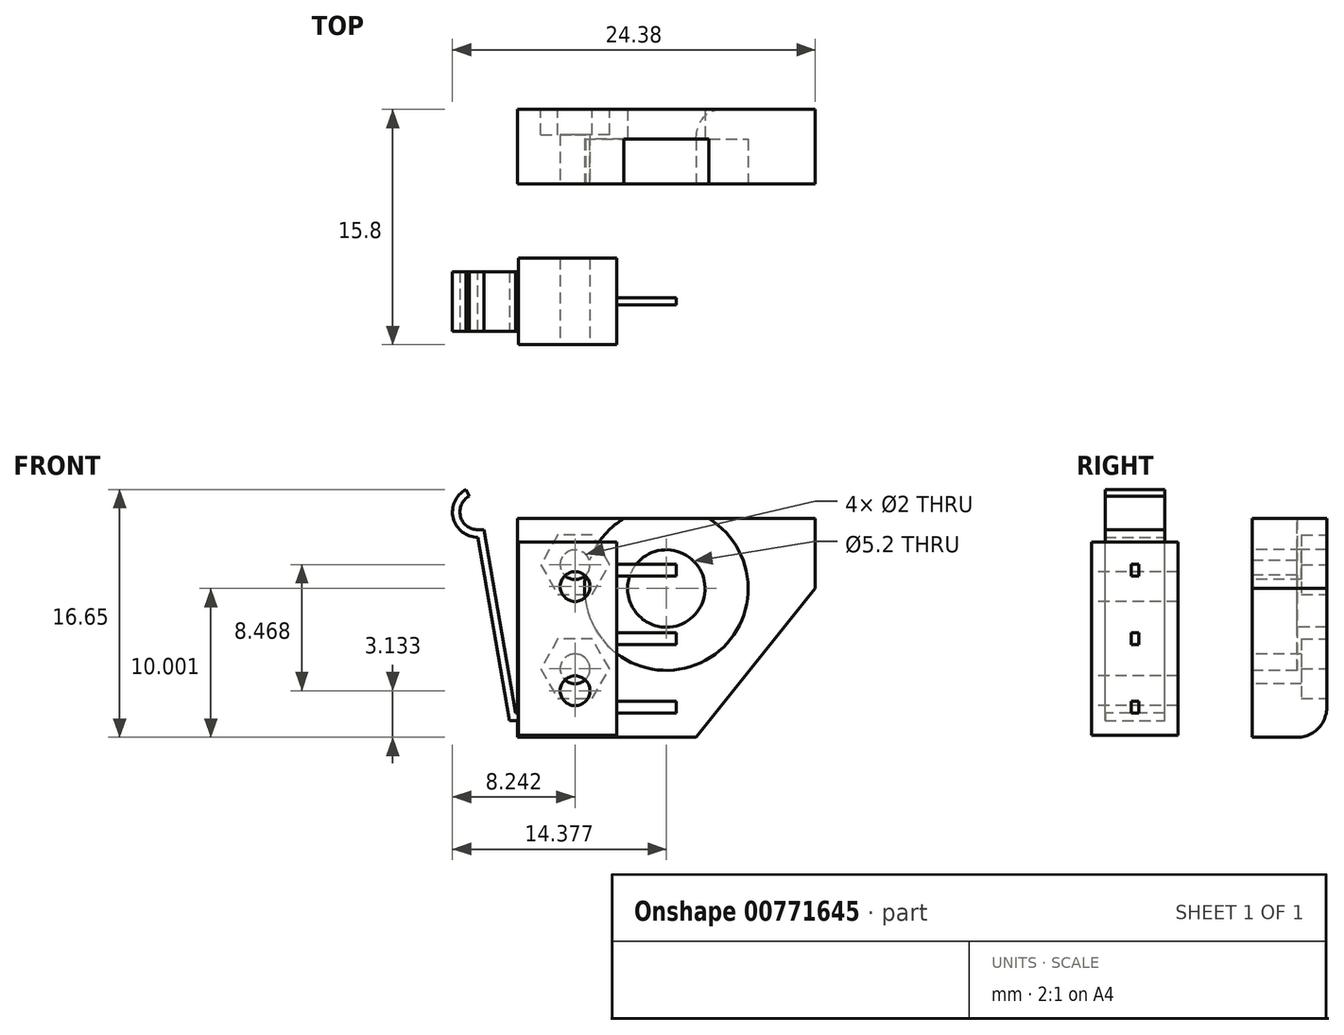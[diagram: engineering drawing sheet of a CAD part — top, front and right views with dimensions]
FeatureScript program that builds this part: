
annotation { "Feature Type Name" : "Feature", "Feature Type Description" : "" }
export const myFeature = defineFeature(function(context is Context, id is Id, definition is map)
    precondition{}
    {
        {
            var Q0;
            Q0=qCreatedBy(makeId("Front.planeOp"),FACE);
            var sketch = newSketch(context, id + "F0", { "sketchPlane" : qUnion([Q0])});
            skLineSegment(sketch, "E0.bottom", {"start": v(-3.96, 2) * mm, "end": v(2.64, 2) * mm});
            skLineSegment(sketch, "E0.top", {"start": v(-3.96, -11) * mm, "end": v(2.64, -11) * mm});
            skLineSegment(sketch, "E0.left", {"start": v(-3.96, 2) * mm, "end": v(-3.96, -11) * mm});
            skLineSegment(sketch, "E0.right", {"start": v(2.64, 2) * mm, "end": v(2.64, -11) * mm});
            skSolve(sketch);
        }
        {
            var Q0;
            Q0 = qSketchRegion(id + "F0", true);
            extrude(context, id + "F1", {"entities" : qUnion([Q0]), "depth" : 5.8 * mm, "offsetDistance" : 25 * mm});
        }
        {
            var Q0;
            Q0=makeQuery(id+"F1.opExtrude","CAP_FACE",FACE,{"disambiguationData":[OSD([sQuery(id+"F0.wireOp",EDGE,"E0.bottom"),sQuery(id+"F0.wireOp",EDGE,"E0.top"),sQuery(id+"F0.wireOp",EDGE,"E0.left"),sQuery(id+"F0.wireOp",EDGE,"E0.right")])],"isStart":false});
            var sketch = newSketch(context, id + "F2", { "sketchPlane" : qUnion([Q0])});
            skCircle(sketch, "E1", {"center": v(-0.16, -1) * mm, "radius": 1 * mm});
            skCircle(sketch, "E2", {"center": v(-0.16, -8) * mm, "radius": 1 * mm});
            skSolve(sketch);
        }
        {
            var Q0;
            Q0 = qSketchRegion(id + "F2", true);
            extrude(context, id + "F3", {"entities" : qUnion([Q0]), "operationType" : NewBodyOperationType.REMOVE, "endBound" : BoundingType.UP_TO_NEXT, "oppositeDirection" : true, "depth" : 25 * mm, "offsetDistance" : 25 * mm});
        }
        {
            var Q0;
            Q0=makeQuery(id+"F1.opExtrude","SWEPT_FACE",FACE,{"disambiguationData":[OSD([sQuery(id+"F0.wireOp",EDGE,"E0.right")])]});
            var sketch = newSketch(context, id + "F4", { "sketchPlane" : qUnion([Q0])});
            skLineSegment(sketch, "E3.bottom", {"start": v(-3.15, 0.5) * mm, "end": v(-2.65, 0.5) * mm});
            skLineSegment(sketch, "E3.top", {"start": v(-3.15, -0.3) * mm, "end": v(-2.65, -0.3) * mm});
            skLineSegment(sketch, "E3.left", {"start": v(-3.15, 0.5) * mm, "end": v(-3.15, -0.3) * mm});
            skLineSegment(sketch, "E3.right", {"start": v(-2.65, 0.5) * mm, "end": v(-2.65, -0.3) * mm});
            skLineSegment(sketch, "E4.bottom", {"start": v(-3.15, -4.1) * mm, "end": v(-2.65, -4.1) * mm});
            skLineSegment(sketch, "E4.top", {"start": v(-3.15, -4.9) * mm, "end": v(-2.65, -4.9) * mm});
            skLineSegment(sketch, "E4.left", {"start": v(-3.15, -4.1) * mm, "end": v(-3.15, -4.9) * mm});
            skLineSegment(sketch, "E4.right", {"start": v(-2.65, -4.1) * mm, "end": v(-2.65, -4.9) * mm});
            skLineSegment(sketch, "E5.bottom", {"start": v(-3.15, -8.7) * mm, "end": v(-2.65, -8.7) * mm});
            skLineSegment(sketch, "E5.top", {"start": v(-3.15, -9.5) * mm, "end": v(-2.65, -9.5) * mm});
            skLineSegment(sketch, "E5.left", {"start": v(-3.15, -8.7) * mm, "end": v(-3.15, -9.5) * mm});
            skLineSegment(sketch, "E5.right", {"start": v(-2.65, -8.7) * mm, "end": v(-2.65, -9.5) * mm});
            skSolve(sketch);
        }
        {
            var Q0;
            Q0 = qSketchRegion(id + "F4", true);
            extrude(context, id + "F5", {"entities" : qUnion([Q0]), "operationType" : NewBodyOperationType.ADD, "depth" : 4 * mm, "offsetDistance" : 25 * mm});
        }
        {
            var Q0;
            Q0=makeQuery(id+"F1.opExtrude","SWEPT_FACE",FACE,{"disambiguationData":[OSD([sQuery(id+"F0.wireOp",EDGE,"E0.left")])]});
            var sketch = newSketch(context, id + "F6", { "sketchPlane" : qUnion([Q0])});
            skLineSegment(sketch, "E6.bottom", {"start": v(0.9, -9.5) * mm, "end": v(4.9, -9.5) * mm});
            skLineSegment(sketch, "E6.top", {"start": v(0.9, -10) * mm, "end": v(4.9, -10) * mm});
            skLineSegment(sketch, "E6.left", {"start": v(0.9, -9.5) * mm, "end": v(0.9, -10) * mm});
            skLineSegment(sketch, "E6.right", {"start": v(4.9, -9.5) * mm, "end": v(4.9, -10) * mm});
            skSolve(sketch);
        }
        {
            var Q0;
            Q0=qCreatedBy(makeId("Front.planeOp"),FACE);
            var sketch = newSketch(context, id + "F7", { "sketchPlane" : qUnion([Q0])});
            skLineSegment(sketch, "E7", {"start": v(-3.56, -10) * mm, "end": v(-4.56, -10) * mm});
            skLineSegment(sketch, "E8", {"start": v(-4.56, -10) * mm, "end": v(-6.7, 2.3) * mm});
            skArc(sketch, "E9", {"start": v(-7.5, 5.5) * mm, "mid": v(-8.35, 3.6) * mm, "end": v(-6.7, 2.3) * mm});
            skSolve(sketch);
        }
        {
            var Q0;
            Q0=makeQuery(id+"F6.imprint","IMPRINT",FACE,{"disambiguationData":[TD([[makeQuery(id+"F6.imprint","IMPRINT",EDGE,{"derivedFrom":sQuery(id+"F6.wireOp",EDGE,"E6.bottom")}),-1.0]])]});
            var Q1;
            Q1 = qConstructionFilter(qBodyType(qCreatedBy(id + "F7" ,EDGE), BodyType.WIRE), ConstructionObject.NO);
            sweep(context, id + "F8", {"operationType" : NewBodyOperationType.ADD, "profiles" : qUnion([Q0]), "path" : qUnion([Q1])});
        }
        {
            var Q0;
            Q0=qCreatedBy(makeId("Front.planeOp"),FACE);
            cPlane(context, id + "F9", {"entities" : qUnion([Q0]), "cplaneType" : CPlaneType.OFFSET, "offset" : 10 * mm, "oppositeDirection" : true, "width" : 150 * mm, "height" : 150 * mm});
        }
        {
            var Q0;
            Q0=qCreatedBy(id+"F9.planeOp",FACE);
            var sketch = newSketch(context, id + "F10", { "sketchPlane" : qUnion([Q0])});
            skLineSegment(sketch, "E10.bottom", {"start": v(-4.02, 3.56) * mm, "end": v(15.98, 3.56) * mm});
            skLineSegment(sketch, "E10.top", {"start": v(-4.02, -11.14) * mm, "end": v(15.98, -11.14) * mm});
            skLineSegment(sketch, "E10.left", {"start": v(-4.02, 3.56) * mm, "end": v(-4.02, -11.14) * mm});
            skLineSegment(sketch, "E10.right", {"start": v(15.98, 3.56) * mm, "end": v(15.98, -11.14) * mm});
            skSolve(sketch);
        }
        {
            var Q0;
            Q0 = qSketchRegion(id + "F10", true);
            extrude(context, id + "F11", {"entities" : qUnion([Q0]), "operationType" : NewBodyOperationType.ADD, "depth" : 5 * mm, "offsetDistance" : 25 * mm});
        }
        {
            var Q0;
            Q0=makeQuery(id+"F11.opExtrude","CAP_FACE",FACE,{"disambiguationData":[OSD([sQuery(id+"F10.wireOp",EDGE,"E10.bottom"),sQuery(id+"F10.wireOp",EDGE,"E10.top"),sQuery(id+"F10.wireOp",EDGE,"E10.left"),sQuery(id+"F10.wireOp",EDGE,"E10.right")])],"isStart":false});
            var sketch = newSketch(context, id + "F12", { "sketchPlane" : qUnion([Q0])});
            skCircle(sketch, "E11", {"center": v(5.98, -1.14) * mm, "radius": 2.6 * mm});
            skSolve(sketch);
        }
        {
            var Q0;
            Q0 = qSketchRegion(id + "F12", true);
            extrude(context, id + "F13", {"entities" : qUnion([Q0]), "operationType" : NewBodyOperationType.REMOVE, "endBound" : BoundingType.UP_TO_NEXT, "oppositeDirection" : true, "depth" : 25 * mm, "offsetDistance" : 25 * mm});
        }
        {
            var Q0;
            Q0=makeQuery(id+"F11.opExtrude","CAP_FACE",FACE,{"disambiguationData":[OSD([sQuery(id+"F10.wireOp",EDGE,"E10.bottom"),sQuery(id+"F10.wireOp",EDGE,"E10.top"),sQuery(id+"F10.wireOp",EDGE,"E10.left"),sQuery(id+"F10.wireOp",EDGE,"E10.right")])],"isStart":false});
            var sketch = newSketch(context, id + "F14", { "sketchPlane" : qUnion([Q0])});
            skCircle(sketch, "E12", {"center": v(5.98, -1.14) * mm, "radius": 5.5 * mm});
            skSolve(sketch);
        }
        {
            var Q0;
            Q0 = qSketchRegion(id + "F14", true);
            extrude(context, id + "F15", {"entities" : qUnion([Q0]), "operationType" : NewBodyOperationType.REMOVE, "oppositeDirection" : true, "depth" : 3 * mm, "offsetDistance" : 25 * mm});
        }
        {
            var Q0;
            Q0=makeQuery(id+"F11.opExtrude","CAP_FACE",FACE,{"disambiguationData":[OSD([sQuery(id+"F10.wireOp",EDGE,"E10.bottom"),sQuery(id+"F10.wireOp",EDGE,"E10.top"),sQuery(id+"F10.wireOp",EDGE,"E10.left"),sQuery(id+"F10.wireOp",EDGE,"E10.right")])],"isStart":false});
            var sketch = newSketch(context, id + "F16", { "sketchPlane" : qUnion([Q0])});
            skCircle(sketch, "E13", {"center": v(-0.16, 0.46) * mm, "radius": 1 * mm});
            skCircle(sketch, "E14", {"center": v(-0.16, -6.54) * mm, "radius": 1 * mm});
            skSolve(sketch);
        }
        {
            var Q0;
            Q0 = qSketchRegion(id + "F16", true);
            extrude(context, id + "F17", {"entities" : qUnion([Q0]), "operationType" : NewBodyOperationType.REMOVE, "endBound" : BoundingType.UP_TO_NEXT, "oppositeDirection" : true, "depth" : 25 * mm, "offsetDistance" : 25 * mm});
        }
        {
            var Q0;
            Q0=makeQuery(id+"F11.opExtrude","CAP_FACE",FACE,{"disambiguationData":[OSD([sQuery(id+"F10.wireOp",EDGE,"E10.bottom"),sQuery(id+"F10.wireOp",EDGE,"E10.top"),sQuery(id+"F10.wireOp",EDGE,"E10.left"),sQuery(id+"F10.wireOp",EDGE,"E10.right")])],"isStart":true});
            var sketch = newSketch(context, id + "F18", { "sketchPlane" : qUnion([Q0])});
            skCircle(sketch, "E15.cCircle", {"center": v(0.16, 0.46) * mm, "radius": 2 * mm, "construction": true});
            skLineSegment(sketch, "E15.0", {"start": v(2.47, 0.46) * mm, "end": v(1.31, -1.54) * mm});
            skLineSegment(sketch, "E15.1", {"start": v(1.31, -1.54) * mm, "end": v(-1, -1.54) * mm});
            skLineSegment(sketch, "E15.2", {"start": v(-1, -1.54) * mm, "end": v(-2.15, 0.46) * mm});
            skLineSegment(sketch, "E15.3", {"start": v(-2.15, 0.46) * mm, "end": v(-1, 2.46) * mm});
            skLineSegment(sketch, "E15.4", {"start": v(-1, 2.46) * mm, "end": v(1.31, 2.46) * mm});
            skLineSegment(sketch, "E15.5", {"start": v(1.31, 2.46) * mm, "end": v(2.47, 0.46) * mm});
            skPoint(sketch, "E15.0.midPoint", {"position": v(1.89, -0.54) * mm});
            skCircle(sketch, "E16.cCircle", {"center": v(0.16, -6.54) * mm, "radius": 2 * mm, "construction": true});
            skLineSegment(sketch, "E16.0", {"start": v(2.47, -6.54) * mm, "end": v(1.31, -8.54) * mm});
            skLineSegment(sketch, "E16.1", {"start": v(1.31, -8.54) * mm, "end": v(-1, -8.54) * mm});
            skLineSegment(sketch, "E16.2", {"start": v(-1, -8.54) * mm, "end": v(-2.15, -6.54) * mm});
            skLineSegment(sketch, "E16.3", {"start": v(-2.15, -6.54) * mm, "end": v(-1, -4.54) * mm});
            skLineSegment(sketch, "E16.4", {"start": v(-1, -4.54) * mm, "end": v(1.31, -4.54) * mm});
            skLineSegment(sketch, "E16.5", {"start": v(1.31, -4.54) * mm, "end": v(2.47, -6.54) * mm});
            skPoint(sketch, "E16.0.midPoint", {"position": v(1.89, -7.54) * mm});
            skSolve(sketch);
        }
        {
            var Q0;
            Q0 = qSketchRegion(id + "F18", true);
            extrude(context, id + "F19", {"entities" : qUnion([Q0]), "operationType" : NewBodyOperationType.REMOVE, "oppositeDirection" : true, "depth" : 1.7 * mm, "offsetDistance" : 25 * mm});
        }
        {
            var Q0;
            Q0=makeQuery(id+"F11.opExtrude","SWEPT_EDGE",EDGE,{"disambiguationData":[OSD([sQuery(id+"F10.wireOp",EDGE,"E10.top"),sQuery(id+"F10.wireOp",EDGE,"E10.right")])]});
            chamfer(context, id + "F20", {"entities" : qUnion([Q0]), "chamferType" : ChamferType.TWO_OFFSETS, "width1" : 10 * mm, "oppositeDirection" : false, "width2" : 8 * mm, "tangentPropagation" : true});
        }
        {
            var Q0;
            Q0=makeQuery(id+"F11.opExtrude","CAP_EDGE",EDGE,{"disambiguationData":[OSD([sQuery(id+"F10.wireOp",EDGE,"E10.top")])],"isStart":true});
            fillet(context, id + "F21", {"entities" : qUnion([Q0]), "radius" : 2 * mm, "tangentPropagation" : true, "allowEdgeOverflow" : false});
        }
    });
